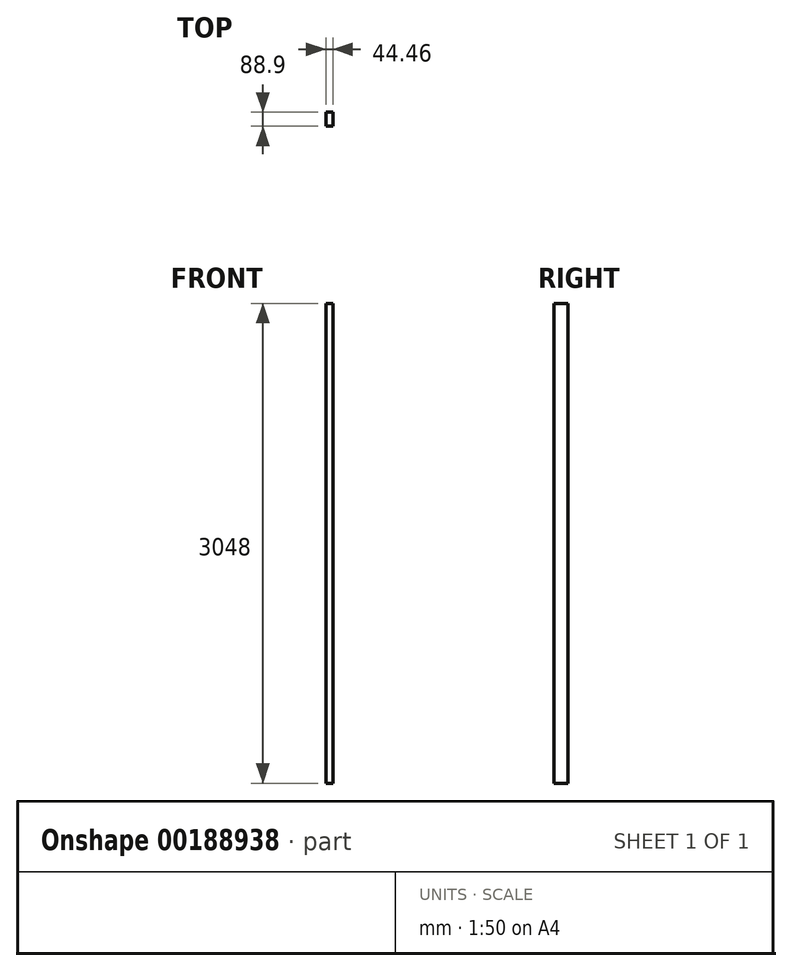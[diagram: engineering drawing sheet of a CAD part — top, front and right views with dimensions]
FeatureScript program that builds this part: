
annotation { "Feature Type Name" : "Feature", "Feature Type Description" : "" }
export const myFeature = defineFeature(function(context is Context, id is Id, definition is map)
    precondition{}
    {
        {
            var Q0;
            Q0=qCreatedBy(makeId("Top.planeOp"),FACE);
            var sketch = newSketch(context, id + "F1", { "sketchPlane" : qUnion([Q0])});
            skLineSegment(sketch, "E0.bottom", {"start": v(22.23, -44.45) * mm, "end": v(-22.22, -44.45) * mm});
            skLineSegment(sketch, "E0.top", {"start": v(22.22, 44.45) * mm, "end": v(-22.23, 44.45) * mm});
            skLineSegment(sketch, "E0.left", {"start": v(22.23, -44.45) * mm, "end": v(22.22, 44.45) * mm});
            skLineSegment(sketch, "E0.right", {"start": v(-22.22, -44.45) * mm, "end": v(-22.23, 44.45) * mm});
            skPoint(sketch, "E0.middle", {"position": v(0, 0) * mm});
            skSolve(sketch);
        }
        {
            var Q0;
            Q0=makeQuery(id+"F1.imprint","IMPRINT",FACE,{"disambiguationData":[TD([[makeQuery(id+"F1.imprint","IMPRINT",EDGE,{"derivedFrom":sQuery(id+"F1.wireOp",EDGE,"E0.bottom")}),-1.0]])]});
            extrude(context, id + "F0", {"entities" : qUnion([Q0]), "endBound" : BoundingType.SYMMETRIC, "depth" : 3048 * mm});
        }
    });
